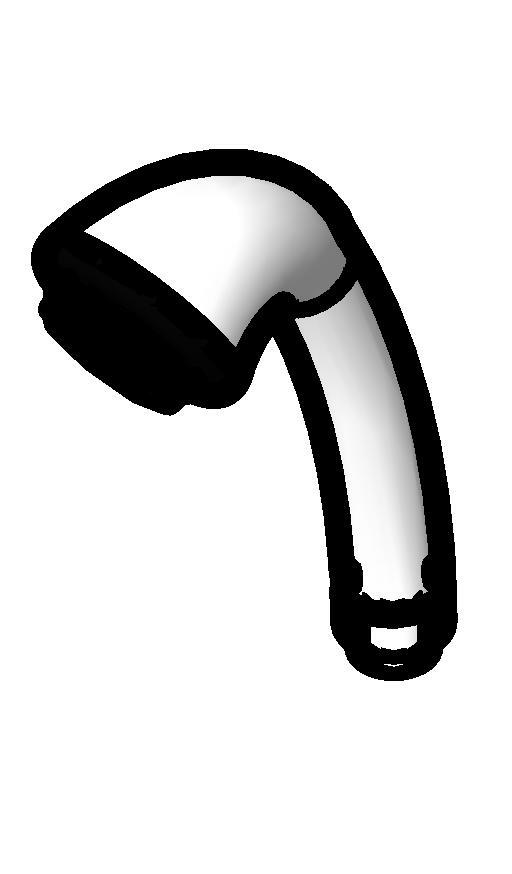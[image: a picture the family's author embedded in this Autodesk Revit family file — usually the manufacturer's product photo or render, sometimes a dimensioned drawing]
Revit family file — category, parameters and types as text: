
# Revit family: Deca_Ducha Manual Max_4892.C
name_source: partatom
category: Plumbing Fixtures
revit_build: Autodesk Revit Architecture 2012 (Build: 20120126_0600(x64)
units: mm (PartAtom-declared; Revit-internal decimal feet)

## types (1)
- 4892.C_Cromado CR10
    Aprovado por = Contino/quattroD
    Assembly Code = D2010700
    Atendimento ao Cliente = 0800-0117073
    Consumo = Varia com a pressão (consultar catálogo)
    Criado por = Contino/quattroD
    Código = 4892.C
    Default Elevation = 2000 mm  [stored 6.56168 ft]
    Description = Ducha  manual
    Diâmetro Ponto de Agua = 15 mm  [stored 0.0492126 ft]
    Ducha Manual = Deca CR10 Cromado Metal
    Flow Pressure = 0.00 psi
    HWFU = 0
    Informações Complementares = Recomendável com pressão mínima de 4 m.c.a para aquecedor de passagem e de 2 m.c.a. para aquecedor de acumulação.
    Linha = Max
    Louça/Metais = Metal
    Manufacturer = Deca
    Material = Deca_Latão Cromado e Plástico de Engenharia
    Model = 4892.C
    Norma = ABNT NBR 15206:2005
    Peso Liquido (Kg) = 0.1
    Pressão = 2 a 40 mca
    Produto = Ducha manual Max
    Raio Ponto de Agua = 8 mm  [stored 0.0262467 ft]
    Segmento = Competitivo
    URL = www.deca.com.br/produtos
    Variações de COR = Cromado (4892.C)
    WFU = 0

note: [stored X ft] marks values corroborated as IEEE doubles in the binary element streams (Revit-internal decimal feet)

## geometry (parser evidence)
native form markers: Blend x4, Sweep x1
no freeform markers — native parametric forms only
